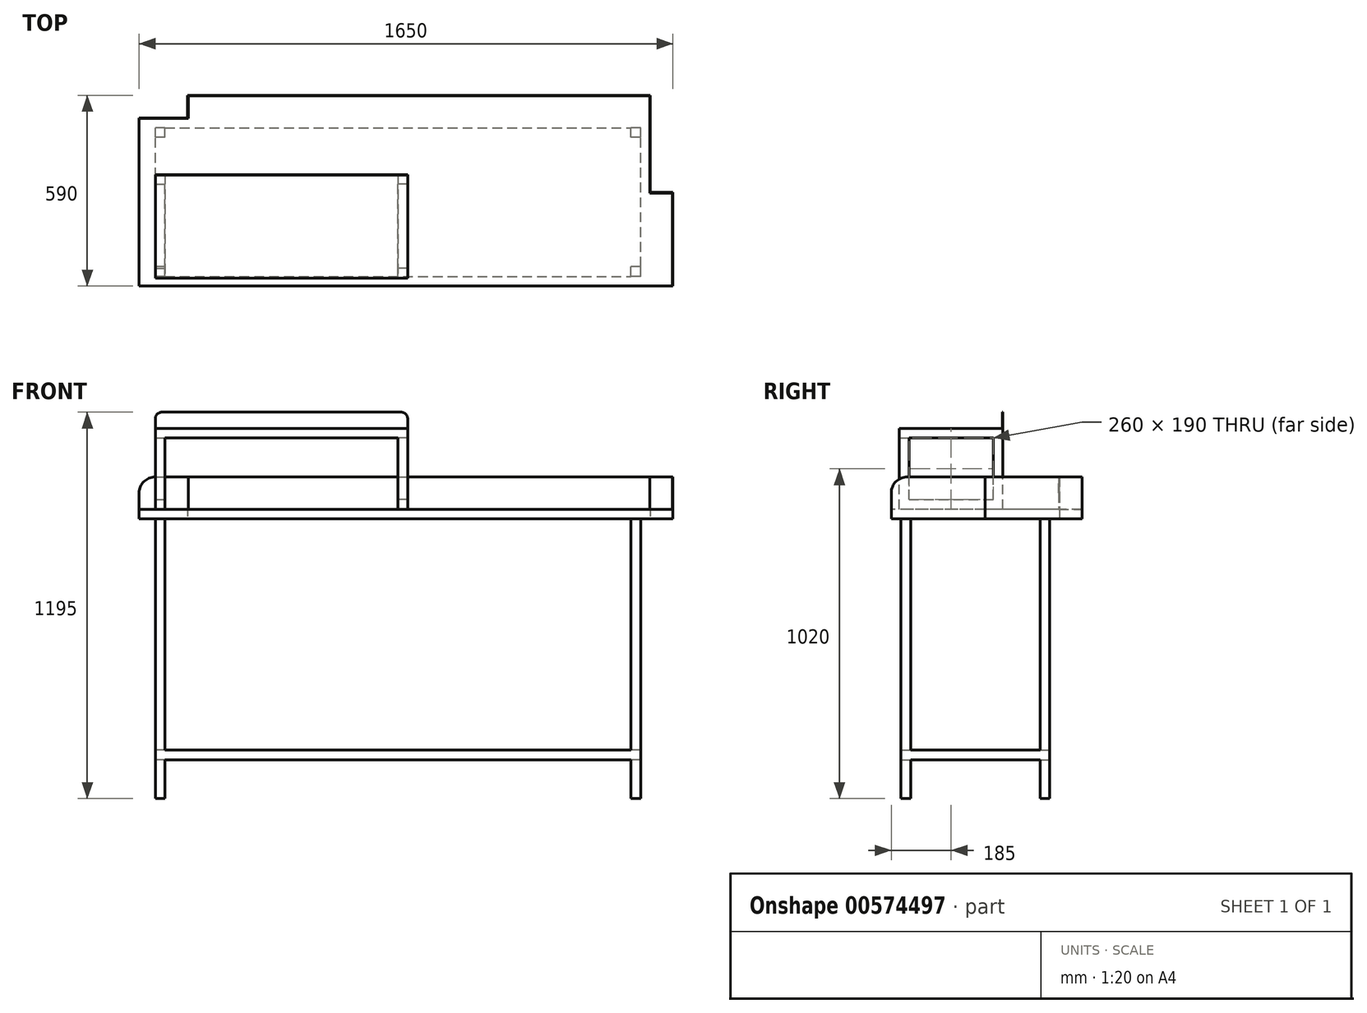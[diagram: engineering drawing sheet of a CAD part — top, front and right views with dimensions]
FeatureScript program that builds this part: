
annotation { "Feature Type Name" : "Feature", "Feature Type Description" : "" }
export const myFeature = defineFeature(function(context is Context, id is Id, definition is map)
    precondition{}
    {
        {
            var Q0;
            Q0=qCreatedBy(makeId("Top.planeOp"),FACE);
            var sketch = newSketch(context, id + "F0", { "sketchPlane" : qUnion([Q0])});
            skLineSegment(sketch, "E0", {"start": v(0, 0) * mm, "end": v(1650, 0) * mm});
            skLineSegment(sketch, "E1", {"start": v(1650, 0) * mm, "end": v(1650, 290) * mm});
            skLineSegment(sketch, "E2", {"start": v(1650, 290) * mm, "end": v(1580, 290) * mm});
            skLineSegment(sketch, "E3", {"start": v(1580, 290) * mm, "end": v(1580, 590) * mm});
            skLineSegment(sketch, "E4", {"start": v(1580, 590) * mm, "end": v(150, 590) * mm});
            skLineSegment(sketch, "E5", {"start": v(0, 520) * mm, "end": v(0, 0) * mm});
            skLineSegment(sketch, "E6", {"start": v(0, 520) * mm, "end": v(150, 520) * mm});
            skLineSegment(sketch, "E7", {"start": v(150, 520) * mm, "end": v(150, 590) * mm});
            skSolve(sketch);
        }
        {
            var Q0;
            Q0 = qSketchRegion(id + "F0", true);
            extrude(context, id + "F1", {"entities" : qUnion([Q0]), "depth" : 30 * mm, "offsetDistance" : 25 * mm});
        }
        {
            var Q0;
            Q0=makeQuery(id+"F1.opExtrude","CAP_FACE",FACE,{"disambiguationData":[OSD([sQuery(id+"F0.wireOp",EDGE,"E0"),sQuery(id+"F0.wireOp",EDGE,"E1"),sQuery(id+"F0.wireOp",EDGE,"E2"),sQuery(id+"F0.wireOp",EDGE,"E3"),sQuery(id+"F0.wireOp",EDGE,"E4"),sQuery(id+"F0.wireOp",EDGE,"E5")])],"isStart":false});
            var sketch = newSketch(context, id + "F2", { "sketchPlane" : qUnion([Q0])});
            skLineSegment(sketch, "E8", {"start": v(1650, 0) * mm, "end": v(1650, 290) * mm});
            skLineSegment(sketch, "E9", {"start": v(1650, 290) * mm, "end": v(1580, 290) * mm});
            skLineSegment(sketch, "E10", {"start": v(1580, 290) * mm, "end": v(1580, 590) * mm});
            skLineSegment(sketch, "E11", {"start": v(1580, 590) * mm, "end": v(150, 590) * mm});
            skLineSegment(sketch, "E12", {"start": v(150, 590) * mm, "end": v(150, 520) * mm});
            skLineSegment(sketch, "E13", {"start": v(150, 520) * mm, "end": v(0, 520) * mm});
            skLineSegment(sketch, "E14", {"start": v(0, 520) * mm, "end": v(0, 518) * mm});
            skLineSegment(sketch, "E15", {"start": v(0, 518) * mm, "end": v(152, 518) * mm});
            skLineSegment(sketch, "E16", {"start": v(152, 518) * mm, "end": v(152, 588) * mm});
            skLineSegment(sketch, "E17", {"start": v(152, 588) * mm, "end": v(1578, 588) * mm});
            skLineSegment(sketch, "E18", {"start": v(1578, 588) * mm, "end": v(1578, 288) * mm});
            skLineSegment(sketch, "E19", {"start": v(1578, 288) * mm, "end": v(1648, 288) * mm});
            skLineSegment(sketch, "E20", {"start": v(1648, 288) * mm, "end": v(1648, 0) * mm});
            skLineSegment(sketch, "E21", {"start": v(1648, 0) * mm, "end": v(1650, 0) * mm});
            skSolve(sketch);
        }
        {
            var Q0;
            Q0 = qSketchRegion(id + "F2", true);
            extrude(context, id + "F3", {"entities" : qUnion([Q0]), "operationType" : NewBodyOperationType.ADD, "depth" : 100 * mm, "offsetDistance" : 25 * mm});
        }
        {
            var Q0;
            Q0=makeQuery(id+"F3.opExtrude","CAP_EDGE",EDGE,{"disambiguationData":[OSD([sQuery(id+"F2.wireOp",EDGE,"E14")])],"isStart":false});
            var Q1;
            Q1=makeQuery(id+"F3.opExtrude","CAP_EDGE",EDGE,{"disambiguationData":[OSD([sQuery(id+"F2.wireOp",EDGE,"E21")])],"isStart":false});
            fillet(context, id + "F4", {"entities" : qUnion([Q0, Q1]), "radius" : 50 * mm, "tangentPropagation" : true, "allowEdgeOverflow" : false});
        }
        {
            var Q0;
            Q0=makeQuery(id+"F1.opExtrude","CAP_FACE",FACE,{"disambiguationData":[OSD([sQuery(id+"F0.wireOp",EDGE,"E0"),sQuery(id+"F0.wireOp",EDGE,"E1"),sQuery(id+"F0.wireOp",EDGE,"E2"),sQuery(id+"F0.wireOp",EDGE,"E3"),sQuery(id+"F0.wireOp",EDGE,"E4"),sQuery(id+"F0.wireOp",EDGE,"E5")])],"isStart":true});
            var sketch = newSketch(context, id + "F5", { "sketchPlane" : qUnion([Q0])});
            skLineSegment(sketch, "E22.bottom", {"start": v(80, -30) * mm, "end": v(50, -30) * mm});
            skLineSegment(sketch, "E22.top", {"start": v(80, -60) * mm, "end": v(50, -60) * mm});
            skLineSegment(sketch, "E22.left", {"start": v(80, -30) * mm, "end": v(80, -60) * mm});
            skLineSegment(sketch, "E22.right", {"start": v(50, -30) * mm, "end": v(50, -60) * mm});
            skPoint(sketch, "E22.middle", {"position": v(65, -45) * mm});
            skLineSegment(sketch, "E23.bottom", {"start": v(1550, -30) * mm, "end": v(1520, -30) * mm});
            skLineSegment(sketch, "E23.top", {"start": v(1550, -60) * mm, "end": v(1520, -60) * mm});
            skLineSegment(sketch, "E23.left", {"start": v(1550, -30) * mm, "end": v(1550, -60) * mm});
            skLineSegment(sketch, "E23.right", {"start": v(1520, -30) * mm, "end": v(1520, -60) * mm});
            skPoint(sketch, "E23.middle", {"position": v(1535, -45) * mm});
            skLineSegment(sketch, "E24.bottom", {"start": v(1550, -460) * mm, "end": v(1520, -460) * mm});
            skLineSegment(sketch, "E24.top", {"start": v(1550, -490) * mm, "end": v(1520, -490) * mm});
            skLineSegment(sketch, "E24.left", {"start": v(1550, -460) * mm, "end": v(1550, -490) * mm});
            skLineSegment(sketch, "E24.right", {"start": v(1520, -460) * mm, "end": v(1520, -490) * mm});
            skPoint(sketch, "E24.middle", {"position": v(1535, -475) * mm});
            skLineSegment(sketch, "E25.bottom", {"start": v(80, -460) * mm, "end": v(50, -460) * mm});
            skLineSegment(sketch, "E25.top", {"start": v(80, -490) * mm, "end": v(50, -490) * mm});
            skLineSegment(sketch, "E25.left", {"start": v(80, -460) * mm, "end": v(80, -490) * mm});
            skLineSegment(sketch, "E25.right", {"start": v(50, -460) * mm, "end": v(50, -490) * mm});
            skPoint(sketch, "E25.middle", {"position": v(65, -475) * mm});
            skPoint(sketch, "E25.middle.positionSnap0", {"position": v(65, -60) * mm});
            skPoint(sketch, "E25.cornerSnap0", {"position": v(1535, -460) * mm});
            skPoint(sketch, "E25.centerSnap0", {"position": v(65, -60) * mm});
            skSolve(sketch);
        }
        {
            var Q0;
            Q0 = qSketchRegion(id + "F5", true);
            extrude(context, id + "F6", {"entities" : qUnion([Q0]), "operationType" : NewBodyOperationType.ADD, "depth" : 865 * mm, "offsetDistance" : 25 * mm});
        }
        {
            var Q0;
            Q0=makeQuery(id+"F6.opExtrude","CAP_FACE",FACE,{"disambiguationData":[OSD([sQuery(id+"F5.wireOp",EDGE,"E22.bottom"),sQuery(id+"F5.wireOp",EDGE,"E22.top"),sQuery(id+"F5.wireOp",EDGE,"E22.left"),sQuery(id+"F5.wireOp",EDGE,"E22.right")])],"isStart":false});
            cPlane(context, id + "F7", {"entities" : qUnion([Q0]), "cplaneType" : CPlaneType.OFFSET, "offset" : 150 * mm, "oppositeDirection" : true, "width" : 150 * mm, "height" : 150 * mm});
        }
        {
            var Q0;
            Q0=qCreatedBy(id+"F7.planeOp",FACE);
            var sketch = newSketch(context, id + "F8", { "sketchPlane" : qUnion([Q0])});
            skLineSegment(sketch, "E26.bottom", {"start": v(50, -30) * mm, "end": v(1550, -30) * mm});
            skLineSegment(sketch, "E26.top", {"start": v(50, -490) * mm, "end": v(1550, -490) * mm});
            skLineSegment(sketch, "E26.left", {"start": v(50, -30) * mm, "end": v(50, -490) * mm});
            skLineSegment(sketch, "E26.right", {"start": v(1550, -30) * mm, "end": v(1550, -490) * mm});
            skSolve(sketch);
        }
        {
            var Q0;
            Q0 = qSketchRegion(id + "F8", true);
            extrude(context, id + "F9", {"entities" : qUnion([Q0]), "operationType" : NewBodyOperationType.ADD, "depth" : 30 * mm, "offsetDistance" : 25 * mm});
        }
        {
            var Q0;
            Q0=makeQuery(id+"F1.opExtrude","CAP_FACE",FACE,{"disambiguationData":[OSD([sQuery(id+"F0.wireOp",EDGE,"E0"),sQuery(id+"F0.wireOp",EDGE,"E1"),sQuery(id+"F0.wireOp",EDGE,"E2"),sQuery(id+"F0.wireOp",EDGE,"E3"),sQuery(id+"F0.wireOp",EDGE,"E4"),sQuery(id+"F0.wireOp",EDGE,"E5")])],"isStart":false});
            cPlane(context, id + "F10", {"entities" : qUnion([Q0]), "cplaneType" : CPlaneType.OFFSET, "offset" : 250 * mm, "width" : 150 * mm, "height" : 150 * mm});
        }
        {
            var Q0;
            Q0=qCreatedBy(id+"F10.planeOp",FACE);
            var sketch = newSketch(context, id + "F11", { "sketchPlane" : qUnion([Q0])});
            skLineSegment(sketch, "E27.bottom", {"start": v(50, 345) * mm, "end": v(830, 345) * mm});
            skLineSegment(sketch, "E27.top", {"start": v(50, 25) * mm, "end": v(830, 25) * mm});
            skLineSegment(sketch, "E27.left", {"start": v(50, 345) * mm, "end": v(50, 25) * mm});
            skLineSegment(sketch, "E27.right", {"start": v(830, 345) * mm, "end": v(830, 25) * mm});
            skSolve(sketch);
        }
        {
            var Q0;
            Q0 = qSketchRegion(id + "F11", true);
            extrude(context, id + "F12", {"entities" : qUnion([Q0]), "oppositeDirection" : true, "depth" : 30 * mm, "offsetDistance" : 25 * mm});
        }
        {
            var Q0;
            Q0=makeQuery(id+"F12.opExtrude","CAP_FACE",FACE,{"disambiguationData":[OSD([sQuery(id+"F11.wireOp",EDGE,"E27.bottom"),sQuery(id+"F11.wireOp",EDGE,"E27.top"),sQuery(id+"F11.wireOp",EDGE,"E27.left"),sQuery(id+"F11.wireOp",EDGE,"E27.right")])],"isStart":false});
            var sketch = newSketch(context, id + "F13", { "sketchPlane" : qUnion([Q0])});
            skLineSegment(sketch, "E28.bottom", {"start": v(50, -25) * mm, "end": v(80, -25) * mm});
            skLineSegment(sketch, "E28.top", {"start": v(50, -55) * mm, "end": v(80, -55) * mm});
            skLineSegment(sketch, "E28.left", {"start": v(50, -25) * mm, "end": v(50, -55) * mm});
            skLineSegment(sketch, "E28.right", {"start": v(80, -25) * mm, "end": v(80, -55) * mm});
            skLineSegment(sketch, "E29.bottom", {"start": v(50, -345) * mm, "end": v(80, -345) * mm});
            skLineSegment(sketch, "E29.top", {"start": v(50, -315) * mm, "end": v(80, -315) * mm});
            skLineSegment(sketch, "E29.left", {"start": v(50, -345) * mm, "end": v(50, -315) * mm});
            skLineSegment(sketch, "E29.right", {"start": v(80, -345) * mm, "end": v(80, -315) * mm});
            skLineSegment(sketch, "E30.bottom", {"start": v(830, -25) * mm, "end": v(800, -25) * mm});
            skLineSegment(sketch, "E30.top", {"start": v(830, -55) * mm, "end": v(800, -55) * mm});
            skLineSegment(sketch, "E30.left", {"start": v(830, -25) * mm, "end": v(830, -55) * mm});
            skLineSegment(sketch, "E30.right", {"start": v(800, -25) * mm, "end": v(800, -55) * mm});
            skLineSegment(sketch, "E31.bottom", {"start": v(830, -345) * mm, "end": v(800, -345) * mm});
            skLineSegment(sketch, "E31.top", {"start": v(830, -315) * mm, "end": v(800, -315) * mm});
            skLineSegment(sketch, "E31.left", {"start": v(830, -345) * mm, "end": v(830, -315) * mm});
            skLineSegment(sketch, "E31.right", {"start": v(800, -345) * mm, "end": v(800, -315) * mm});
            skSolve(sketch);
        }
        {
            var Q0;
            Q0 = qSketchRegion(id + "F13", true);
            extrude(context, id + "F14", {"entities" : qUnion([Q0]), "operationType" : NewBodyOperationType.ADD, "endBound" : BoundingType.UP_TO_NEXT, "depth" : 25 * mm, "offsetDistance" : 25 * mm});
        }
        {
            var Q0;
            Q0=makeQuery(id+"F14.opExtrude","SWEPT_FACE",FACE,{"disambiguationData":[OSD([sQuery(id+"F13.wireOp",EDGE,"E29.top")])]});
            var sketch = newSketch(context, id + "F15", { "sketchPlane" : qUnion([Q0])});
            skLineSegment(sketch, "E32.bottom", {"start": v(50, 30) * mm, "end": v(80, 30) * mm});
            skLineSegment(sketch, "E32.top", {"start": v(50, 60) * mm, "end": v(80, 60) * mm});
            skLineSegment(sketch, "E32.left", {"start": v(50, 30) * mm, "end": v(50, 60) * mm});
            skLineSegment(sketch, "E32.right", {"start": v(80, 30) * mm, "end": v(80, 60) * mm});
            skLineSegment(sketch, "E33.bottom", {"start": v(830, 30) * mm, "end": v(800, 30) * mm});
            skLineSegment(sketch, "E33.top", {"start": v(830, 60) * mm, "end": v(800, 60) * mm});
            skLineSegment(sketch, "E33.left", {"start": v(830, 30) * mm, "end": v(830, 60) * mm});
            skLineSegment(sketch, "E33.right", {"start": v(800, 30) * mm, "end": v(800, 60) * mm});
            skSolve(sketch);
        }
        {
            var Q0;
            Q0 = qSketchRegion(id + "F15", true);
            extrude(context, id + "F16", {"entities" : qUnion([Q0]), "operationType" : NewBodyOperationType.ADD, "endBound" : BoundingType.UP_TO_NEXT, "depth" : 25 * mm, "offsetDistance" : 25 * mm});
        }
        {
            var Q0;
            Q0=makeQuery(id+"F12.opExtrude","CAP_FACE",FACE,{"disambiguationData":[OSD([sQuery(id+"F11.wireOp",EDGE,"E27.bottom"),sQuery(id+"F11.wireOp",EDGE,"E27.top"),sQuery(id+"F11.wireOp",EDGE,"E27.left"),sQuery(id+"F11.wireOp",EDGE,"E27.right")])],"isStart":true});
            var sketch = newSketch(context, id + "F17", { "sketchPlane" : qUnion([Q0])});
            skLineSegment(sketch, "E34.bottom", {"start": v(50, 345) * mm, "end": v(830, 345) * mm});
            skLineSegment(sketch, "E34.top", {"start": v(50, 343) * mm, "end": v(830, 343) * mm});
            skLineSegment(sketch, "E34.left", {"start": v(50, 345) * mm, "end": v(50, 343) * mm});
            skLineSegment(sketch, "E34.right", {"start": v(830, 345) * mm, "end": v(830, 343) * mm});
            skSolve(sketch);
        }
        {
            var Q0;
            Q0 = qSketchRegion(id + "F17", true);
            extrude(context, id + "F18", {"entities" : qUnion([Q0]), "operationType" : NewBodyOperationType.ADD, "depth" : 50 * mm, "offsetDistance" : 25 * mm});
        }
        {
            var Q0;
            Q0=makeQuery(id+"F18.opExtrude","CAP_EDGE",EDGE,{"disambiguationData":[OSD([sQuery(id+"F17.wireOp",EDGE,"E34.left")])],"isStart":false});
            var Q1;
            Q1=makeQuery(id+"F18.opExtrude","CAP_EDGE",EDGE,{"disambiguationData":[OSD([sQuery(id+"F17.wireOp",EDGE,"E34.right")])],"isStart":false});
            fillet(context, id + "F19", {"entities" : qUnion([Q0, Q1]), "radius" : 20 * mm, "tangentPropagation" : true, "allowEdgeOverflow" : false});
        }
    });
